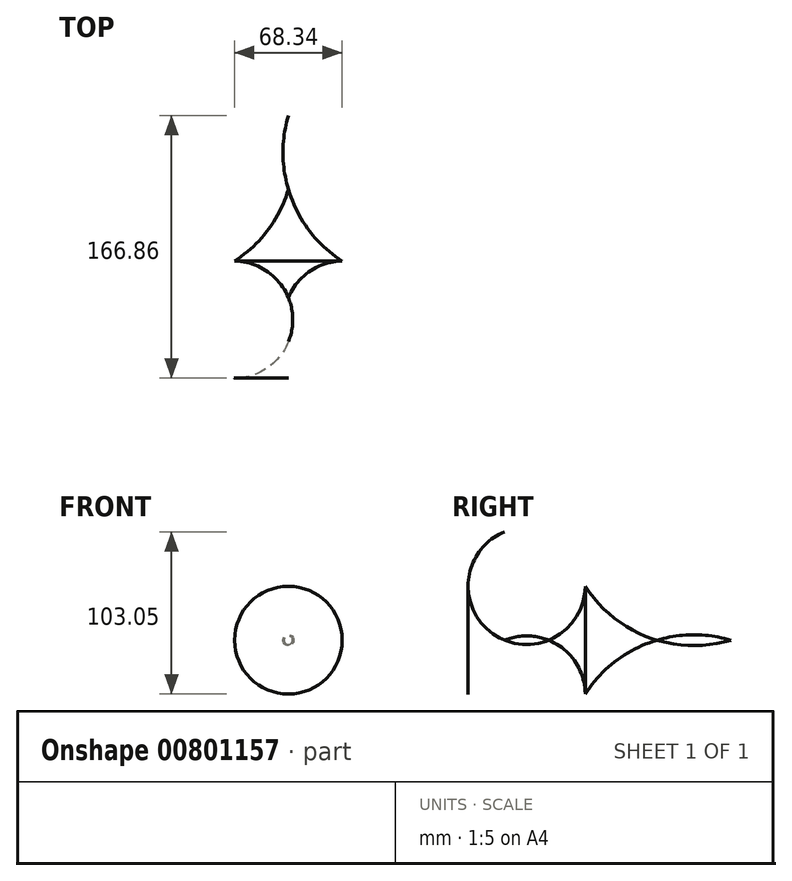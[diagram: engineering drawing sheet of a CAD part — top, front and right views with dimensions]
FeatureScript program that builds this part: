
annotation { "Feature Type Name" : "Feature", "Feature Type Description" : "" }
export const myFeature = defineFeature(function(context is Context, id is Id, definition is map)
    precondition{}
    {
        {
            var Q0;
            Q0=qCreatedBy(makeId("Top.planeOp"),FACE);
            var sketch = newSketch(context, id + "F0", { "sketchPlane" : qUnion([Q0])});
            skLineSegment(sketch, "E0", {"start": v(0, 74.89) * mm, "end": v(0, -74.69) * mm, "construction": true});
            skArc(sketch, "E1", {"start": v(34.17, -2.97) * mm, "mid": v(13.57, -9.38) * mm, "end": v(0, -26.15) * mm});
            skArc(sketch, "E2", {"start": v(0, 42.6) * mm, "mid": v(13.01, 16.76) * mm, "end": v(34.17, -2.97) * mm});
            skLineSegment(sketch, "E3", {"start": v(0, 42.6) * mm, "end": v(0, -26.15) * mm});
            skSolve(sketch);
        }
        {
            var Q0;
            Q0 = qSketchRegion(id + "F0", true);
            var Q1;
            Q1=sQuery(id+"F0.wireOp",EDGE,"E0");
            revolve(context, id + "F1", {"surfaceOperationType" : NewSurfaceOperationType.NEW, "entities" : qUnion([Q0]), "axis" : qUnion([Q1]), "revolveType" : RevolveType.FULL});
        }
    });
